# Revit family: Electronics_Huddle-Room-Solutions_Biamp_Devio_Beamtracking-Ceiling-Microphone_DCM-1__
name_source: partatom
category: Communication Devices
units: mm (PartAtom-declared; Revit-internal decimal feet)

## family parameters
Cut with Voids When Loaded = No
Host = Face
Maintain Annotation Orientation = No
OmniClass Number = 23.85.10.11.14.14.11
OmniClass Title = Microphones
Part Type = Normal
Room Calculation Point = No
Round Connector Dimension = Use Diameter
Shared = No

## types (2) — shared parameters
Altitude = 0-6,600 ft (0-2000m) MSL
Automatic Noise Suppression = 4 modes: Of, Low (Default), Medium, High
Connector = Custom 2-pin (cable length 10 feet [3 meters])
Default Elevation = 4' - 0"
Depth = 0' - 5 1/2"
Description = Devio® DCM-1 Beamtracking™ Ceiling Microphone
Digital Interface = Custom/Proprietary
Dynamic Range = THD+N < 10%: 92 dB, A-Weighted
Frequency Response = 150 Hz - 16 kHz: ± 3 dB
Height = 0' - 2"
Humidity = 0-95% relative humidity (non-condensing)
Indicators = Mute Indicator (Green/Red LED)
Manufacturer = Biamp
Maximum SPL = 0.5% THD: 106 dB SPL
Microphone Technology = 8-Element Digital Array
Model = Devio DCM-1
Polar Pattern = Active Beamformed
Power = < 1 W, phantom powered from plenum box
Product Documentation Link = https://downloads.biamp.com
Product Page URL = https://www.biamp.com
Product data url = https://www.bimobject.com
Selectable Elevation Modes = 4 modes: multiple 30° selections
Sensitivity = 94 dB SPL, 1 kHz: > 70 dB, A-Weighted
Temperature Range = 32 - 104° F (0 - 40° C)
URL = https://www.biamp.com
Weight = 0.86 lbf
Width = 0' - 4"

## per-type parameters (varying)
| type | Grill Material | Housing Material |
| DCM-1 Black | Biamp - Grill - Black | Biamp - Plastic - Black |
| DCM-1 White | Biamp - Grill - White | Biamp - Plastic - White |

## geometry (parser evidence)
native form markers: Sweep x2
no freeform markers — native parametric forms only
